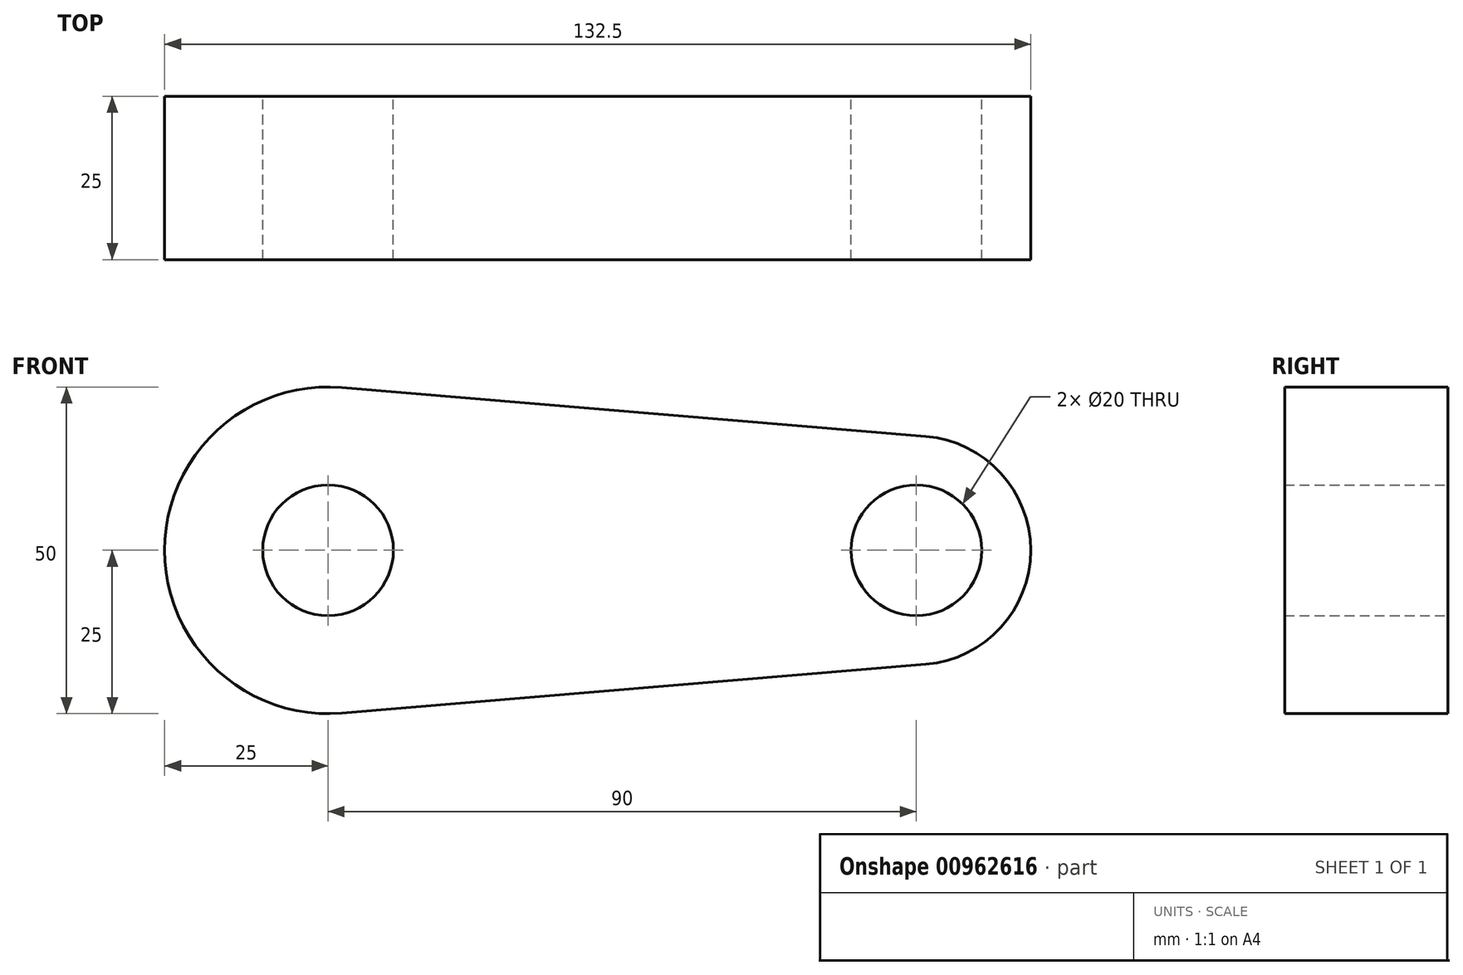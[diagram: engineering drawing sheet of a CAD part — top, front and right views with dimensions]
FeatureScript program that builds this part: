
annotation { "Feature Type Name" : "Feature", "Feature Type Description" : "" }
export const myFeature = defineFeature(function(context is Context, id is Id, definition is map)
    precondition{}
    {
        {
            var Q0;
            Q0=qCreatedBy(makeId("Front.planeOp"),FACE);
            var sketch = newSketch(context, id + "F0", { "sketchPlane" : qUnion([Q0])});
            skCircle(sketch, "E0", {"center": v(0, 0) * mm, "radius": 25 * mm});
            skCircle(sketch, "E1", {"center": v(90, 0) * mm, "radius": 17.5 * mm});
            skCircle(sketch, "E2", {"center": v(0, 0) * mm, "radius": 10 * mm});
            skCircle(sketch, "E3", {"center": v(90, 0) * mm, "radius": 10 * mm});
            skLineSegment(sketch, "E4", {"start": v(2.08, 24.91) * mm, "end": v(91.46, 17.44) * mm});
            skLineSegment(sketch, "E5", {"start": v(2.08, -24.91) * mm, "end": v(91.46, -17.44) * mm});
            skSolve(sketch);
        }
        {
            var Q0;
            Q0=makeQuery(id+"F0.imprint","IMPRINT",FACE,{"disambiguationData":[TD([[makeQuery(id+"F0.imprint","IMPRINT",EDGE,{"derivedFrom":sQuery(id+"F0.wireOp",EDGE,"E2")}),-1.0]])]});
            var Q1;
            {var subQ0=sQuery(id+"F0.wireOp",EDGE,"E4");Q1=makeQuery(id+"F0.imprint","IMPRINT",FACE,{"disambiguationData":[TD([[makeQuery(id+"F0.imprint","IMPRINT",EDGE,{"derivedFrom":subQ0}),-1.0]])]});}
            var Q2;
            Q2=makeQuery(id+"F0.imprint","IMPRINT",FACE,{"disambiguationData":[TD([[makeQuery(id+"F0.imprint","IMPRINT",EDGE,{"derivedFrom":sQuery(id+"F0.wireOp",EDGE,"E3")}),-1.0]])]});
            var Q3;
            Q3=sQuery(id+"F0.wireOp",EDGE,"E1");
            var Q4;
            Q4=sQuery(id+"F0.wireOp",EDGE,"E0");
            var Q5;
            Q5=sQuery(id+"F0.wireOp",EDGE,"E5");
            var Q6;
            Q6=sQuery(id+"F0.wireOp",EDGE,"E4");
            var Q7;
            Q7=sQuery(id+"F0.wireOp",EDGE,"E2");
            var Q8;
            Q8=sQuery(id+"F0.wireOp",EDGE,"E3");
            extrude(context, id + "F1", {"entities" : qUnion([Q0, Q1, Q2]), "surfaceEntities" : qUnion([Q3, Q4, Q5, Q6, Q7, Q8]), "depth" : 25 * mm, "offsetDistance" : 25 * mm});
        }
    });
